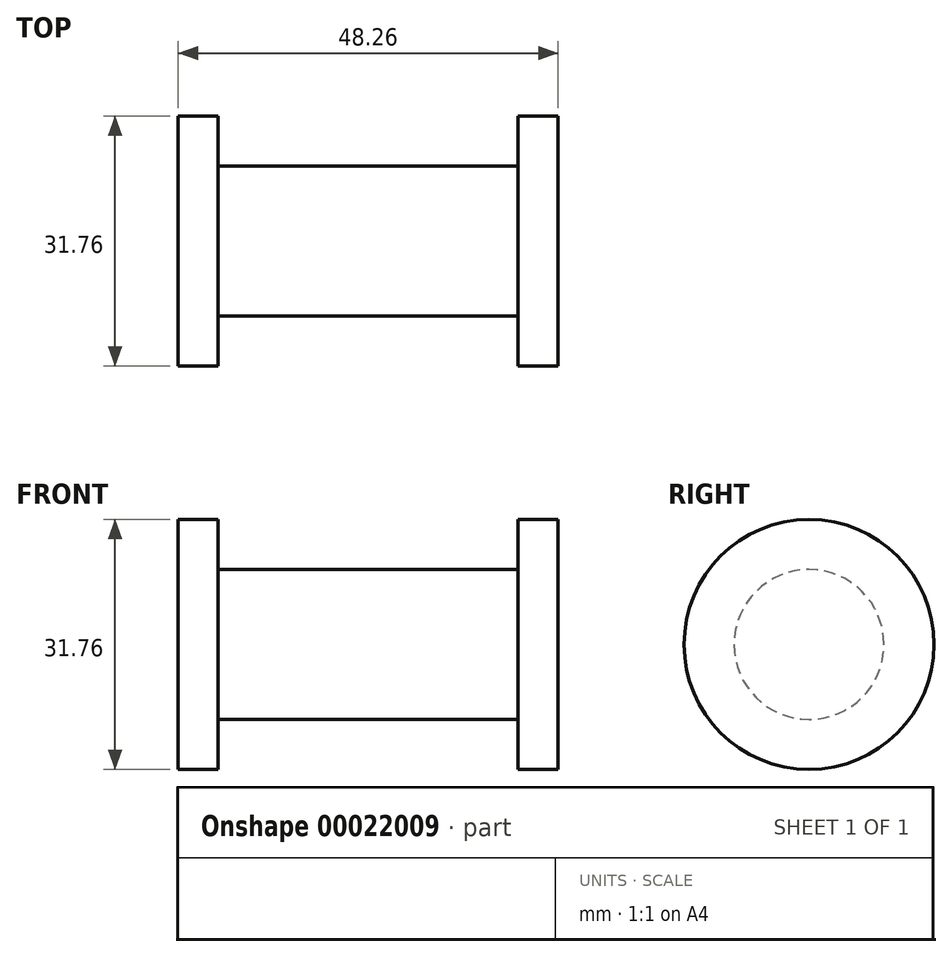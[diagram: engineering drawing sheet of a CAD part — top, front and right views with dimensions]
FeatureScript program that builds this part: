
annotation { "Feature Type Name" : "Feature", "Feature Type Description" : "" }
export const myFeature = defineFeature(function(context is Context, id is Id, definition is map)
    precondition{}
    {
        {
            var Q0;
            Q0=qCreatedBy(makeId("Right.planeOp"),FACE);
            var sketch = newSketch(context, id + "F0", { "sketchPlane" : qUnion([Q0])});
            skCircle(sketch, "E0", {"center": v(0, 0) * mm, "radius": 15.88 * mm});
            skSolve(sketch);
        }
        {
            var Q0;
            Q0 = qSketchRegion(id + "F0", true);
            extrude(context, id + "F1", {"entities" : qUnion([Q0]), "depth" : 5.08 * mm});
        }
        {
            var Q0;
            Q0=makeQuery(id+"F1.opExtrude","CAP_FACE",FACE,{"disambiguationData":[OSD([sQuery(id+"F0.wireOp",EDGE,"E0")])],"isStart":true});
            var sketch = newSketch(context, id + "F2", { "sketchPlane" : qUnion([Q0])});
            skCircle(sketch, "E1", {"center": v(0, 0) * mm, "radius": 9.53 * mm});
            skSolve(sketch);
        }
        {
            var Q0;
            Q0 = qSketchRegion(id + "F2", true);
            extrude(context, id + "F3", {"entities" : qUnion([Q0]), "operationType" : NewBodyOperationType.ADD, "depth" : 38.1 * mm});
        }
        {
            var Q0;
            Q0=makeQuery(id+"F3.opExtrude","CAP_FACE",FACE,{"disambiguationData":[OSD([sQuery(id+"F2.wireOp",EDGE,"E1")])],"isStart":false});
            var sketch = newSketch(context, id + "F4", { "sketchPlane" : qUnion([Q0])});
            skCircle(sketch, "E2", {"center": v(0, 0) * mm, "radius": 15.88 * mm});
            skSolve(sketch);
        }
        {
            var Q0;
            Q0 = qSketchRegion(id + "F4", true);
            extrude(context, id + "F5", {"entities" : qUnion([Q0]), "operationType" : NewBodyOperationType.ADD, "depth" : 5.08 * mm});
        }
    });
